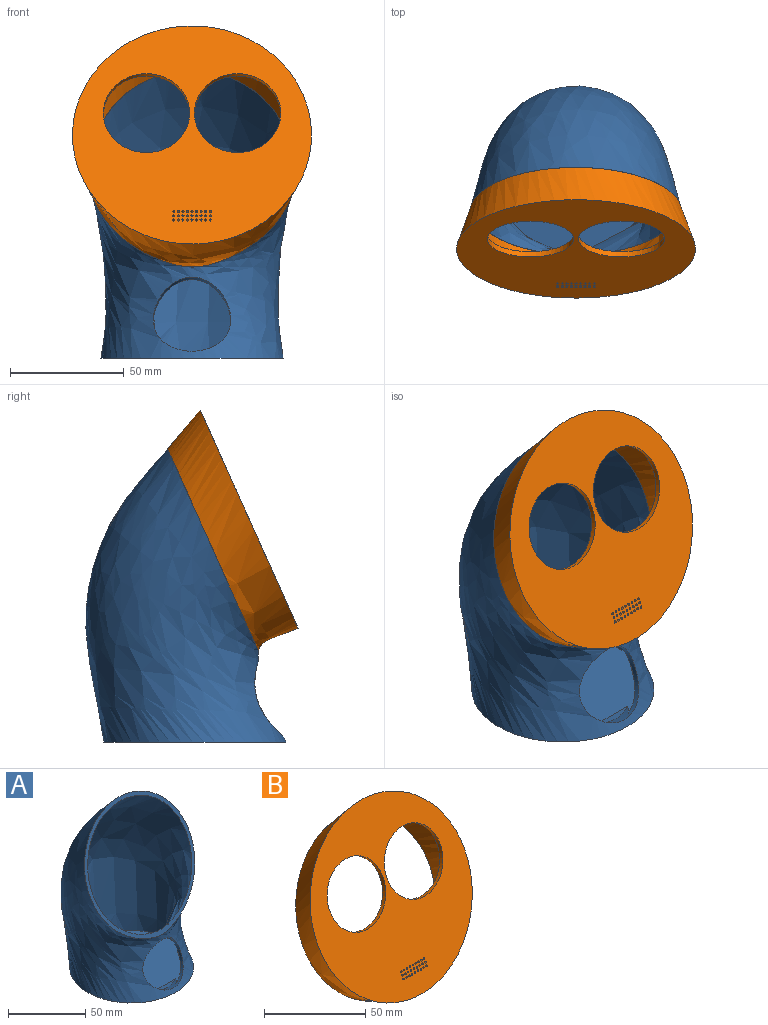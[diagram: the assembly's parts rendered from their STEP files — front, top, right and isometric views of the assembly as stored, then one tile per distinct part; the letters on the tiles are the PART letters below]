
ASSEMBLY  parts=2 mates=1
PART A: 10 faces, bbox 3865.2x3379.3x2772 mm
  f0: plane 2564.68x2560.58mm, normal (0,-0.91,0.41), area 773.2mm2, adj f2,f4
  f1: plane 80x80mm, normal (0,0,-1), area 5026.2mm2, adj f2
  f2: bspline ~145.91x105.22mm, area 21858.2mm2, adj f0,f1,f6
  f3: plane 216.87x216.16mm, normal (0,0,1), area 4226.9mm2, adj f4,f5,f6,f9
  f4: offset ~1392.62x912.43mm, area 452931.1mm2, adj f0,f3,f5,f6,f7,f8
  f5: offset ~60.88x44.62mm, area 140.9mm2, adj f3,f4,f6,f7
  f6: cylinder r=17mm len=35.15mm, axis (0,-0.91,0.41), area 329mm2, adj f2,f3,f4,f5,f7,f8,f9
  f7: plane 7.01x4.62mm, normal (0,-0.91,0.41), area 0.7mm2, adj f4,f5,f6
  f8: plane 1170.15x1166.76mm, normal (0,-0.91,0.41), area 2.1mm2, adj f4,f6
  f9: plane 17.31x2.16mm, normal (0,-0.91,0.41), area 27.8mm2, adj f3,f6
PART B: 34 faces, bbox 660.3x536.2x607.9 mm
  f0: plane 498.75x494.65mm, normal (0,0.91,-0.41), area 772.4mm2, adj f2,f4
  f1: plane 105.05x95.84mm, normal (0,-0.91,0.41), area 6369.5mm2, adj f2,f5,f6,f7,f8,f9,f10,f11
  f2: bspline ~105.87x104.93mm, area 6565mm2, adj f0,f1
  f3: plane 506.94x498.55mm, normal (0,0.91,-0.41), area 5264.8mm2, adj f4,f5,f6,f7,f8,f9,f10,f11
  f4: offset ~253.29x201.93mm, area 10969.5mm2, adj f0,f3
  f5: cylinder r=0.5mm len=2.69mm, axis (0,-0.91,0.41), area 7.9mm2, adj f1,f3
  f6: cylinder r=0.5mm len=2.69mm, axis (0,-0.91,0.41), area 7.9mm2, adj f1,f3
  f7: cylinder r=0.5mm len=2.69mm, axis (0,-0.91,0.41), area 7.9mm2, adj f1,f3
  f8: cylinder r=0.5mm len=2.69mm, axis (0,-0.91,0.41), area 7.9mm2, adj f1,f3
  f9: cylinder r=0.5mm len=2.69mm, axis (0,-0.91,0.41), area 7.9mm2, adj f1,f3
  f10: cylinder r=0.5mm len=2.69mm, axis (0,-0.91,0.41), area 7.9mm2, adj f1,f3
  f11: cylinder r=0.5mm len=2.69mm, axis (0,-0.91,0.41), area 7.9mm2, adj f1,f3
  f12: cylinder r=0.5mm len=2.69mm, axis (0,-0.91,0.41), area 7.9mm2, adj f1,f3
  f13: cylinder r=0.5mm len=2.69mm, axis (0,-0.91,0.41), area 7.9mm2, adj f1,f3
  f14: cylinder r=0.5mm len=2.69mm, axis (0,-0.91,0.41), area 7.9mm2, adj f1,f3
  f15: cylinder r=0.5mm len=2.69mm, axis (0,-0.91,0.41), area 7.9mm2, adj f1,f3
  f16: cylinder r=19mm len=38mm, axis (0,-0.91,0.41), area 298.5mm2, adj f1,f3
  f17: cylinder r=19mm len=38mm, axis (0,-0.91,0.41), area 298.5mm2, adj f1,f3
  f18: cylinder r=0.5mm len=2.69mm, axis (0,-0.91,0.41), area 7.9mm2, adj f1,f3
  f19: cylinder r=0.5mm len=2.69mm, axis (0,-0.91,0.41), area 7.9mm2, adj f1,f3
  f20: cylinder r=0.5mm len=2.69mm, axis (0,-0.91,0.41), area 7.9mm2, adj f1,f3
  f21: cylinder r=0.5mm len=2.69mm, axis (0,-0.91,0.41), area 7.9mm2, adj f1,f3
  f22: cylinder r=0.5mm len=2.69mm, axis (0,-0.91,0.41), area 7.9mm2, adj f1,f3
  f23: cylinder r=0.5mm len=2.69mm, axis (0,-0.91,0.41), area 7.9mm2, adj f1,f3
  f24: cylinder r=0.5mm len=2.69mm, axis (0,-0.91,0.41), area 7.9mm2, adj f1,f3
  f25: cylinder r=0.5mm len=2.69mm, axis (0,-0.91,0.41), area 7.9mm2, adj f1,f3
  f26: cylinder r=0.5mm len=2.69mm, axis (0,-0.91,0.41), area 7.9mm2, adj f1,f3
  f27: cylinder r=0.5mm len=2.69mm, axis (0,-0.91,0.41), area 7.9mm2, adj f1,f3
  f28: cylinder r=0.5mm len=2.69mm, axis (0,-0.91,0.41), area 7.9mm2, adj f1,f3
  f29: cylinder r=0.5mm len=2.69mm, axis (0,-0.91,0.41), area 7.9mm2, adj f1,f3
  f30: cylinder r=0.5mm len=2.69mm, axis (0,-0.91,0.41), area 7.9mm2, adj f1,f3
  f31: cylinder r=0.5mm len=2.69mm, axis (0,-0.91,0.41), area 7.9mm2, adj f1,f3
  f32: cylinder r=0.5mm len=2.69mm, axis (0,-0.91,0.41), area 7.9mm2, adj f1,f3
  f33: cylinder r=0.5mm len=2.69mm, axis (0,-0.91,0.41), area 7.9mm2, adj f1,f3
PLACE A t=(-0.01,-50,0)mm
PLACE B t=(-0.01,0,0.01)mm
MATE fastened A.f0 <-> B.f0  axis (0,-0.91,0.41) through (-0.07,-57.84,84.65)mm
